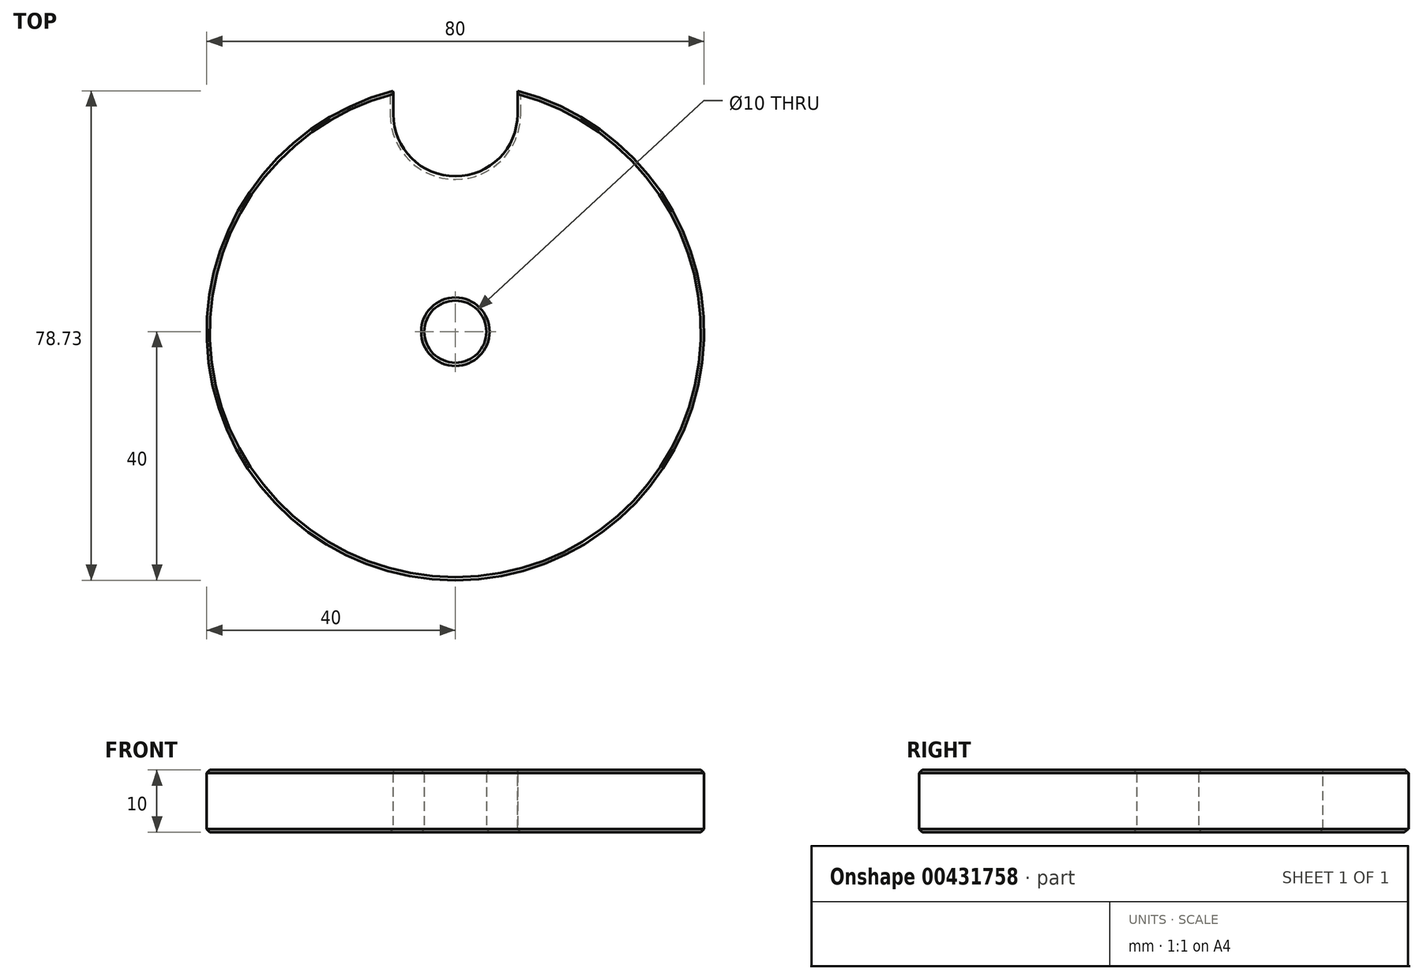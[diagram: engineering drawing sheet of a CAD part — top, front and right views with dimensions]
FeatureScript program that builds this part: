
annotation { "Feature Type Name" : "Feature", "Feature Type Description" : "" }
export const myFeature = defineFeature(function(context is Context, id is Id, definition is map)
    precondition{}
    {
        {
            var Q0;
            Q0=qCreatedBy(makeId("Top.planeOp"),FACE);
            var sketch = newSketch(context, id + "F0", { "sketchPlane" : qUnion([Q0])});
            skCircle(sketch, "E0", {"center": v(0, 0) * mm, "radius": 40 * mm});
            skCircle(sketch, "E1", {"center": v(0, 0) * mm, "radius": 5 * mm});
            skSolve(sketch);
        }
        {
            var Q0;
            Q0 = qSketchRegion(id + "F0", true);
            extrude(context, id + "F1", {"entities" : qUnion([Q0]), "depth" : 10 * mm});
        }
        {
            var Q0;
            Q0=makeQuery(id+"F1.opExtrude","CAP_EDGE",EDGE,{"disambiguationData":[OSD([sQuery(id+"F0.wireOp",EDGE,"E1")])],"isStart":false});
            var Q1;
            Q1=makeQuery(id+"F1.opExtrude","CAP_EDGE",EDGE,{"disambiguationData":[OSD([sQuery(id+"F0.wireOp",EDGE,"E1")])],"isStart":true});
            var Q2;
            Q2=makeQuery(id+"F1.opExtrude","CAP_EDGE",EDGE,{"disambiguationData":[OSD([sQuery(id+"F0.wireOp",EDGE,"E0")])],"isStart":false});
            var Q3;
            Q3=makeQuery(id+"F1.opExtrude","CAP_EDGE",EDGE,{"disambiguationData":[OSD([sQuery(id+"F0.wireOp",EDGE,"E0")])],"isStart":true});
            chamfer(context, id + "F2", {"entities" : qUnion([Q0, Q1, Q2, Q3]), "width" : 0.5 * mm, "tangentPropagation" : true});
        }
        {
            var Q0;
            Q0=makeQuery(id+"F1.opExtrude","CAP_FACE",FACE,{"disambiguationData":[OSD([sQuery(id+"F0.wireOp",EDGE,"E0"),sQuery(id+"F0.wireOp",EDGE,"E1")])],"isStart":false});
            var sketch = newSketch(context, id + "F3", { "sketchPlane" : qUnion([Q0])});
            skArc(sketch, "E2", {"start": v(-10, 34.96) * mm, "mid": v(0.02, 25) * mm, "end": v(10, 35) * mm});
            skLineSegment(sketch, "E3", {"start": v(10, 35) * mm, "end": v(10, 40.76) * mm});
            skLineSegment(sketch, "E4", {"start": v(-10, 34.96) * mm, "end": v(-10.02, 40.68) * mm});
            skLineSegment(sketch, "E5", {"start": v(-10.02, 40.68) * mm, "end": v(10, 40.76) * mm});
            skSolve(sketch);
        }
        {
            var Q0;
            {var subQ0=sQuery(id+"F3.wireOp",EDGE,"E5");Q0=makeQuery(id+"F3.imprint","IMPRINT",FACE,{"disambiguationData":[TD([[makeQuery(id+"F3.imprint","IMPRINT",EDGE,{"derivedFrom":subQ0}),-1.0]])]});}
            var Q1;
            {var subQ0=sQuery(id+"F3.wireOp",EDGE,"E2");Q1=makeQuery(id+"F3.imprint","IMPRINT",FACE,{"disambiguationData":[TD([[makeQuery(id+"F3.imprint","IMPRINT",EDGE,{"derivedFrom":subQ0}),1.0]])]});}
            extrude(context, id + "F4", {"entities" : qUnion([Q0, Q1]), "operationType" : NewBodyOperationType.REMOVE, "endBound" : BoundingType.THROUGH_ALL, "oppositeDirection" : true, "depth" : 25 * mm});
        }
        {
            var Q0;
            Q0=makeQuery(id+"F4.boolean.opBoolean","COPY",EDGE,{"derivedFrom":makeQuery(id+"F4.opExtrude","CAP_EDGE",EDGE,{"disambiguationData":[OSD([sQuery(id+"F3.wireOp",EDGE,"E4")])],"isStart":true})});
            var Q1;
            Q1=makeQuery(id+"F4.boolean.opBoolean","COPY",EDGE,{"derivedFrom":makeQuery(id+"F4.opExtrude","CAP_EDGE",EDGE,{"disambiguationData":[OSD([sQuery(id+"F3.wireOp",EDGE,"E2")])],"isStart":true})});
            var Q2;
            Q2=makeQuery(id+"F4.boolean.opBoolean","COPY",EDGE,{"derivedFrom":makeQuery(id+"F4.opExtrude","CAP_EDGE",EDGE,{"disambiguationData":[OSD([sQuery(id+"F3.wireOp",EDGE,"E3")])],"isStart":true})});
            var Q3;
            Q3=makeQuery(id+"F4.boolean.opBoolean","INTERSECT",EDGE,{"derivedFrom":[makeQuery(id+"F1.opExtrude","CAP_FACE",FACE,{"disambiguationData":[OSD([sQuery(id+"F0.wireOp",EDGE,"E0"),sQuery(id+"F0.wireOp",EDGE,"E1")])],"isStart":true}),makeQuery(id+"F4.opExtrude","SWEPT_FACE",FACE,{"disambiguationData":[OSD([sQuery(id+"F3.wireOp",EDGE,"E3")])]})]});
            var Q4;
            Q4=makeQuery(id+"F4.boolean.opBoolean","INTERSECT",EDGE,{"derivedFrom":[makeQuery(id+"F1.opExtrude","CAP_FACE",FACE,{"disambiguationData":[OSD([sQuery(id+"F0.wireOp",EDGE,"E0"),sQuery(id+"F0.wireOp",EDGE,"E1")])],"isStart":true}),makeQuery(id+"F4.opExtrude","SWEPT_FACE",FACE,{"disambiguationData":[OSD([sQuery(id+"F3.wireOp",EDGE,"E2")])]})]});
            chamfer(context, id + "F5", {"entities" : qUnion([Q0, Q1, Q2, Q3, Q4]), "width" : 0.5 * mm, "tangentPropagation" : true});
        }
    });
